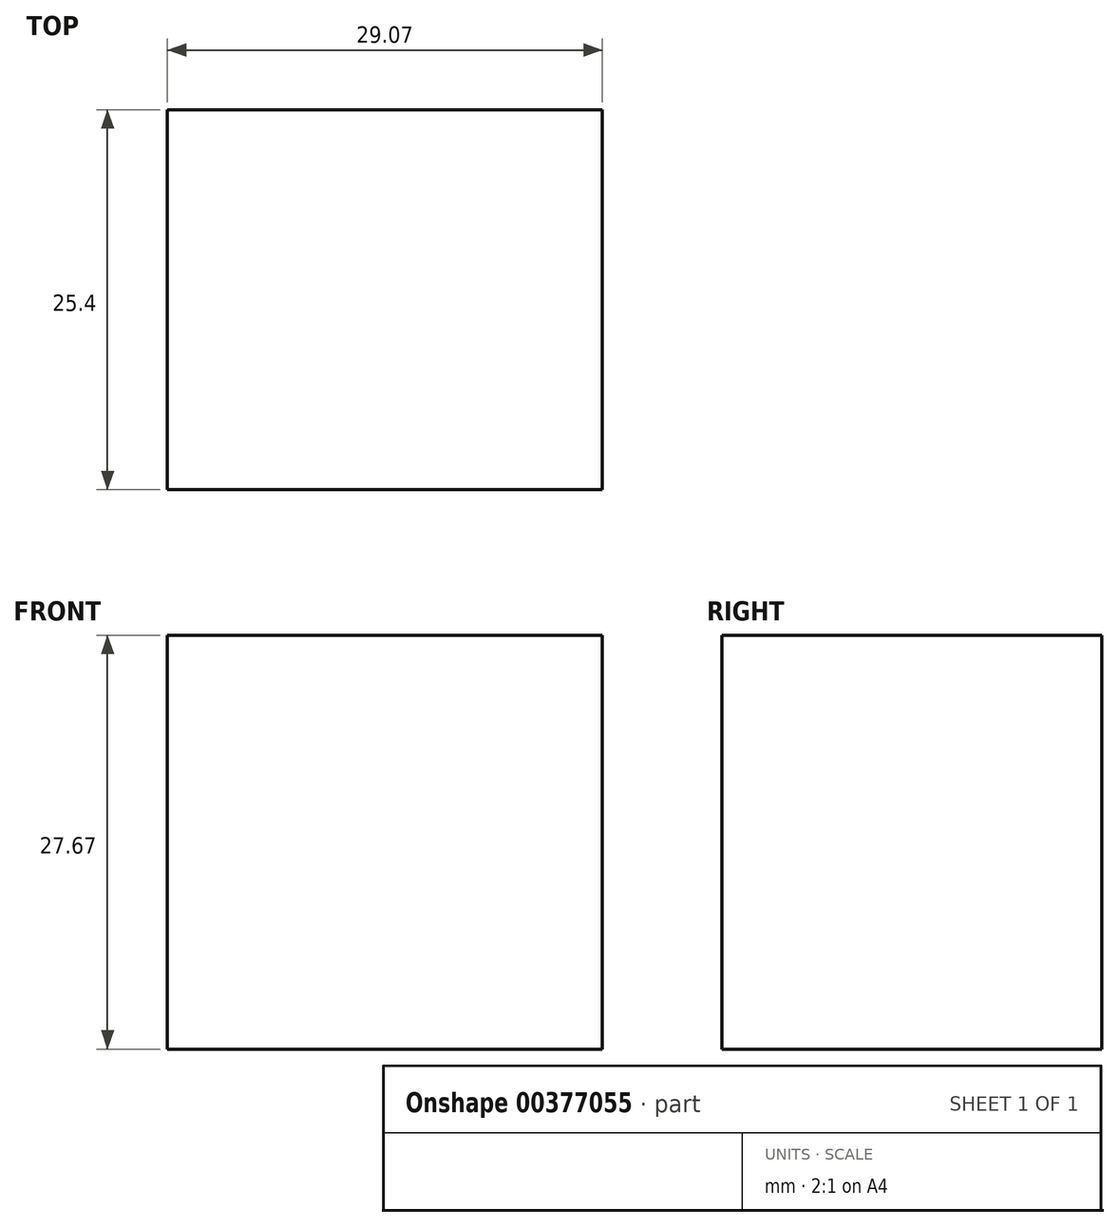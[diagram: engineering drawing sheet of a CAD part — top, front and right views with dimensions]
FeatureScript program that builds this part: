
annotation { "Feature Type Name" : "Feature", "Feature Type Description" : "" }
export const myFeature = defineFeature(function(context is Context, id is Id, definition is map)
    precondition{}
    {
        {
            var Q0;
            Q0=qCreatedBy(makeId("Front.planeOp"),FACE);
            var sketch = newSketch(context, id + "F0", { "sketchPlane" : qUnion([Q0])});
            skLineSegment(sketch, "E0.bottom", {"start": v(-10.47, 11.23) * mm, "end": v(18.6, 11.23) * mm});
            skLineSegment(sketch, "E0.top", {"start": v(-10.47, -16.44) * mm, "end": v(18.6, -16.44) * mm});
            skLineSegment(sketch, "E0.left", {"start": v(-10.47, 11.23) * mm, "end": v(-10.47, -16.44) * mm});
            skLineSegment(sketch, "E0.right", {"start": v(18.6, 11.23) * mm, "end": v(18.6, -16.44) * mm});
            skLineSegment(sketch, "E1", {"start": v(18.6, 11.23) * mm, "end": v(40.34, 25.53) * mm});
            skLineSegment(sketch, "E2", {"start": v(40.34, 25.53) * mm, "end": v(42.75, 8.07) * mm});
            skLineSegment(sketch, "E3", {"start": v(42.75, 8.07) * mm, "end": v(18.6, -16.44) * mm});
            skSolve(sketch);
        }
        {
            var Q0;
            Q0=makeQuery(id+"F0.imprint","IMPRINT",FACE,{"disambiguationData":[TD([[makeQuery(id+"F0.imprint","IMPRINT",EDGE,{"derivedFrom":sQuery(id+"F0.wireOp",EDGE,"E0.bottom")}),-1.0]])]});
            extrude(context, id + "F1", {"entities" : qUnion([Q0]), "depth" : 25.4 * mm});
        }
    });
